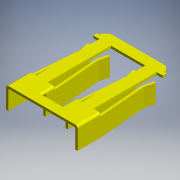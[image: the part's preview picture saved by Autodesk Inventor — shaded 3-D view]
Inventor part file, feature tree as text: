
AUTODESK INVENTOR PART (.ipt)
format: ipt  version: 2017.3 (Build 213256000, 256)  size: 218,112 bytes
history: native  units: mm (DEFAULTED — no unit token found)
features: extrude x7, other x7, sketch x7
ambient origin geometry x8: Origin, YZ Plane, XZ Plane, XY Plane, X Axis, Y Axis, Z Axis, Center Point
bodies: Solid1 (feature_tree)
feature tree (21):
  extrude  "Extrusion1"  Depth=1.27mm TaperAngle=0.0deg
  extrude  "Extrusion2"  Depth=0.762mm TaperAngle=0.0deg
  extrude  "Extrusion3"  Depth=1.016mm TaperAngle=0.0deg
  extrude  "Extrusion4"  [1 undecoded]
  extrude  "Extrusion5"  [1 undecoded]
  extrude  "Extrusion6"  [1 undecoded]
  extrude  "Extrusion7"  [1 undecoded]
  other  "pins_to_body_XY"
  other  "pins_to_body_YZ"
  other  "pins_to_body_ZX"
  other  "pins_to_body_X"
  other  "pins_to_body_Y"
  other  "pins_to_body_Z"
  other  "pins_to_body_Center"
  sketch  "Sketch__1"  dims[d0=0.127mm d1=0.0mm d2=1.27mm d3=0.0mm]
  sketch  "Sketch_1"  dims[d4=1.27mm d5=0.0mm d6=0.762mm d7=0.0mm]
  sketch  "Sketch_2"  dims[d8=1.016mm d9=0.0mm d10=1.016mm d11=0.0mm]
  sketch  "Sketch_3"  dims[d12=1.27mm d13=0.0mm]
  sketch  "Sketch_4"
  sketch  "Sketch_5"
  sketch  "Sketch_6"
note: 4 required parameter values undecoded (feature->parameter linkage not recoverable at this tier; creation-order binding heuristic only, values carry confidence <= 0.55)
